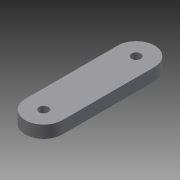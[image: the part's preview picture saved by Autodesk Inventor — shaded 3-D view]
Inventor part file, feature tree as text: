
AUTODESK INVENTOR PART (.ipt)
format: ipt  version: 2013 (Build 170138000, 138)  size: 78,848 bytes
history: native  units: mm
features: extrude x1, sketch x1
ambient origin geometry x8: Origin, YZ Plane, XZ Plane, XY Plane, X Axis, Y Axis, Z Axis, Center Point
bodies: Solid1 (feature_tree)
feature tree (2):
  extrude  "Extrusion1"  Depth=30.0mm
  sketch  "Sketch1"  dims[d0=12.0mm d1=30.0mm d2=3.0mm d3=3.0mm d4=4.0mm d5=0.0mm]
